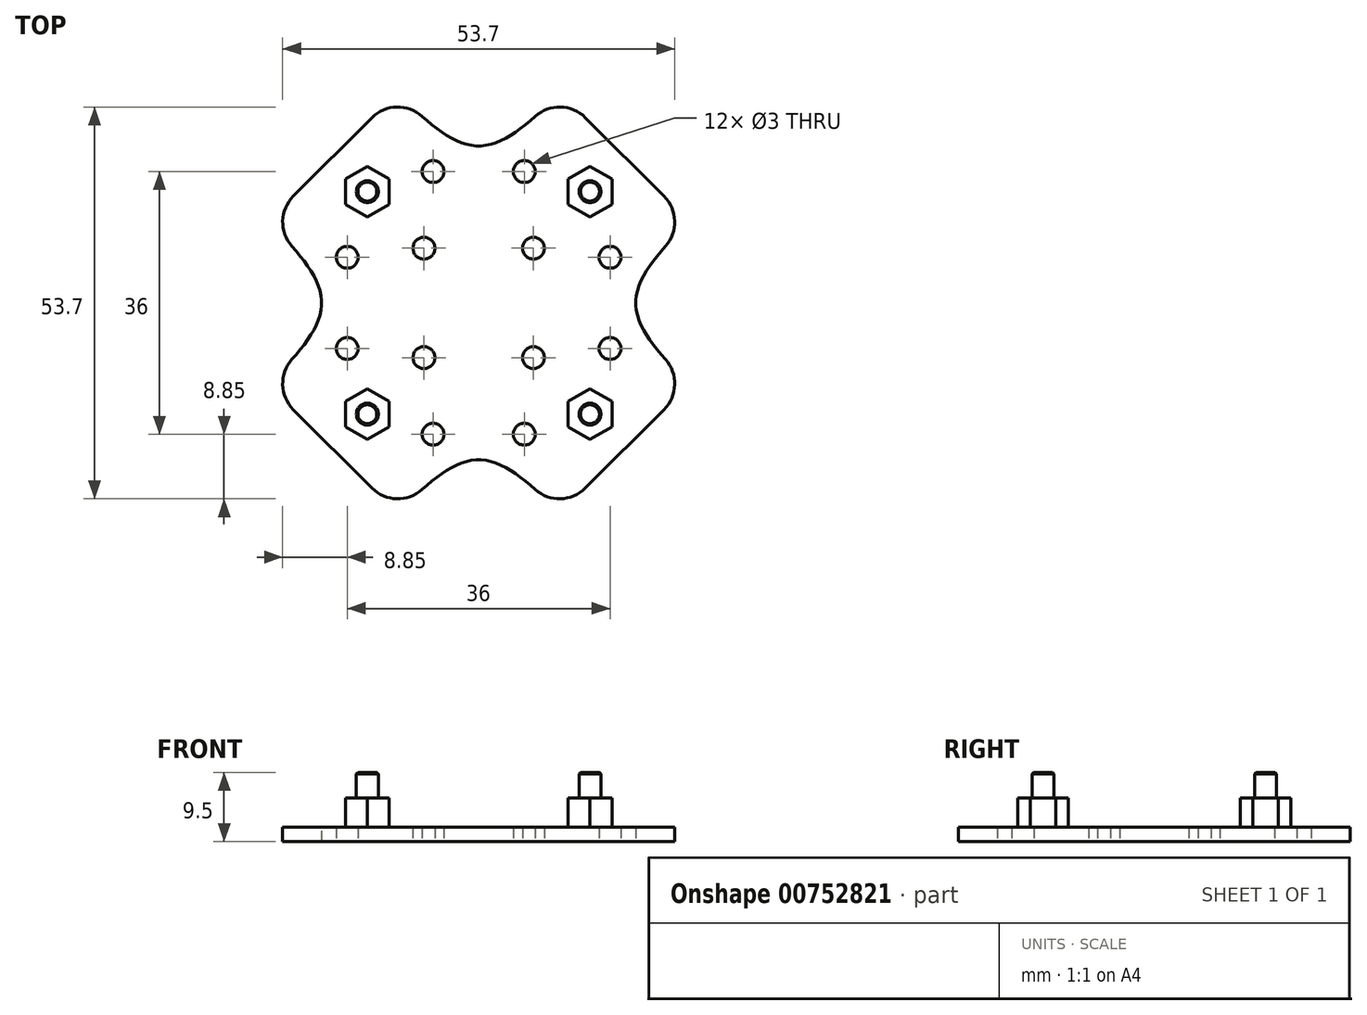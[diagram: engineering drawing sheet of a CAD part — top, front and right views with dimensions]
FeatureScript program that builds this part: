
annotation { "Feature Type Name" : "Feature", "Feature Type Description" : "" }
export const myFeature = defineFeature(function(context is Context, id is Id, definition is map)
    precondition{}
    {
        {
            var Q0;
            Q0=qCreatedBy(makeId("Top.planeOp"),FACE);
            var sketch = newSketch(context, id + "F0", { "sketchPlane" : qUnion([Q0])});
            skLineSegment(sketch, "E0.bottom", {"start": v(18, 18) * mm, "end": v(-18, 18) * mm, "construction": true});
            skLineSegment(sketch, "E0.top", {"start": v(18, -18) * mm, "end": v(-18, -18) * mm, "construction": true});
            skLineSegment(sketch, "E0.left", {"start": v(18, 18) * mm, "end": v(18, -18) * mm, "construction": true});
            skLineSegment(sketch, "E0.right", {"start": v(-18, 18) * mm, "end": v(-18, -18) * mm, "construction": true});
            skPoint(sketch, "E0.middle", {"position": v(0, 0) * mm});
            skLineSegment(sketch, "E1.bottom", {"start": v(15.25, 15.25) * mm, "end": v(-15.25, 15.25) * mm, "construction": true});
            skLineSegment(sketch, "E1.top", {"start": v(15.25, -15.25) * mm, "end": v(-15.25, -15.25) * mm, "construction": true});
            skLineSegment(sketch, "E1.left", {"start": v(15.25, 15.25) * mm, "end": v(15.25, -15.25) * mm, "construction": true});
            skLineSegment(sketch, "E1.right", {"start": v(-15.25, 15.25) * mm, "end": v(-15.25, -15.25) * mm, "construction": true});
            skCircle(sketch, "E2", {"center": v(-15.25, 15.25) * mm, "radius": 1.5 * mm});
            skCircle(sketch, "E3", {"center": v(15.25, 15.25) * mm, "radius": 1.5 * mm});
            skCircle(sketch, "E4", {"center": v(15.25, -15.25) * mm, "radius": 1.5 * mm});
            skCircle(sketch, "E5", {"center": v(-15.25, -15.25) * mm, "radius": 1.5 * mm});
            skLineSegment(sketch, "E6", {"start": v(0, 0) * mm, "end": v(-67.18, 67.18) * mm, "construction": true});
            skLineSegment(sketch, "E7", {"start": v(0, 0) * mm, "end": v(67.18, 67.18) * mm, "construction": true});
            skLineSegment(sketch, "E8", {"start": v(0, 0) * mm, "end": v(-67.18, -67.18) * mm, "construction": true});
            skLineSegment(sketch, "E9", {"start": v(0, 0) * mm, "end": v(67.18, -67.18) * mm, "construction": true});
            skCircle(sketch, "E10", {"center": v(-67.18, 67.18) * mm, "radius": 5 * mm});
            skCircle(sketch, "E11", {"center": v(-75.18, 67.18) * mm, "radius": 1.65 * mm});
            skCircle(sketch, "E12", {"center": v(-67.18, 76.68) * mm, "radius": 1.65 * mm});
            skCircle(sketch, "E13", {"center": v(-59.18, 67.18) * mm, "radius": 1.65 * mm});
            skCircle(sketch, "E14", {"center": v(-67.18, 57.68) * mm, "radius": 1.65 * mm});
            skCircle(sketch, "E15", {"center": v(67.18, 67.18) * mm, "radius": 5 * mm});
            skCircle(sketch, "E16", {"center": v(59.18, 67.18) * mm, "radius": 1.65 * mm});
            skCircle(sketch, "E17", {"center": v(67.18, 76.68) * mm, "radius": 1.65 * mm});
            skCircle(sketch, "E18", {"center": v(75.18, 67.18) * mm, "radius": 1.65 * mm});
            skCircle(sketch, "E19", {"center": v(67.18, 57.68) * mm, "radius": 1.65 * mm});
            skCircle(sketch, "E20", {"center": v(67.18, -67.18) * mm, "radius": 5 * mm});
            skCircle(sketch, "E21", {"center": v(59.18, -67.18) * mm, "radius": 1.65 * mm});
            skCircle(sketch, "E22", {"center": v(67.18, -57.68) * mm, "radius": 1.65 * mm});
            skCircle(sketch, "E23", {"center": v(75.18, -67.18) * mm, "radius": 1.65 * mm});
            skCircle(sketch, "E24", {"center": v(67.18, -76.68) * mm, "radius": 1.65 * mm});
            skCircle(sketch, "E25", {"center": v(-67.18, -67.18) * mm, "radius": 5 * mm});
            skCircle(sketch, "E26", {"center": v(-75.18, -67.18) * mm, "radius": 1.65 * mm});
            skCircle(sketch, "E27", {"center": v(-67.18, -57.68) * mm, "radius": 1.65 * mm});
            skCircle(sketch, "E28", {"center": v(-59.18, -67.18) * mm, "radius": 1.65 * mm});
            skCircle(sketch, "E29", {"center": v(-67.18, -76.68) * mm, "radius": 1.65 * mm});
            skCircle(sketch, "E30", {"center": v(-67.18, 67.18) * mm, "radius": 13.3 * mm, "construction": true});
            skCircle(sketch, "E31", {"center": v(-67.18, 67.18) * mm, "radius": 15.25 * mm});
            skCircle(sketch, "E32", {"center": v(67.18, 67.18) * mm, "radius": 13.3 * mm, "construction": true});
            skCircle(sketch, "E33", {"center": v(67.18, 67.18) * mm, "radius": 15.25 * mm});
            skCircle(sketch, "E34", {"center": v(-67.18, -67.18) * mm, "radius": 13.3 * mm, "construction": true});
            skCircle(sketch, "E35", {"center": v(-67.18, -67.18) * mm, "radius": 15.25 * mm});
            skCircle(sketch, "E36", {"center": v(67.18, -67.18) * mm, "radius": 13.3 * mm, "construction": true});
            skCircle(sketch, "E37", {"center": v(67.18, -67.18) * mm, "radius": 15.25 * mm});
            skLineSegment(sketch, "E38.bottom", {"start": v(20, 20) * mm, "end": v(-20, 20) * mm, "construction": true});
            skLineSegment(sketch, "E38.top", {"start": v(20, -20) * mm, "end": v(-20, -20) * mm, "construction": true});
            skLineSegment(sketch, "E38.left", {"start": v(20, 20) * mm, "end": v(20, -20) * mm, "construction": true});
            skLineSegment(sketch, "E38.right", {"start": v(-20, 20) * mm, "end": v(-20, -20) * mm, "construction": true});
            skLineSegment(sketch, "E39", {"start": v(-67.18, 67.18) * mm, "end": v(-77.96, 56.4) * mm, "construction": true});
            skLineSegment(sketch, "E40", {"start": v(-67.18, 67.18) * mm, "end": v(-56.4, 77.96) * mm, "construction": true});
            skPoint(sketch, "E41", {"position": v(0, 20) * mm});
            skPoint(sketch, "E42", {"position": v(-20, 0) * mm});
            skFitSpline(sketch, "E43", {"points": [v(-77.96, 56.4) * mm, v(-20, 0) * mm], "startDerivative": vector(73.8, -34.55) * mm, "endDerivative": vector(31.31, -75.4) * mm});
            skFitSpline(sketch, "E44", {"points": [v(-56.4, 77.96) * mm, v(0, 20) * mm], "startDerivative": vector(34.55, -73.8) * mm, "endDerivative": vector(75.4, -31.31) * mm});
            skLineSegment(sketch, "E45", {"start": v(67.18, 67.18) * mm, "end": v(56.4, 77.96) * mm, "construction": true});
            skLineSegment(sketch, "E46", {"start": v(67.18, 67.18) * mm, "end": v(77.96, 56.4) * mm, "construction": true});
            skFitSpline(sketch, "E47", {"points": [v(56.4, 77.96) * mm, v(0, 20) * mm], "startDerivative": vector(-34.5, -73.75) * mm, "endDerivative": vector(-75.31, -31.22) * mm});
            skFitSpline(sketch, "E48", {"points": [v(77.96, 56.4) * mm, v(20, 0) * mm], "startDerivative": vector(-73.75, -34.5) * mm, "endDerivative": vector(-31.22, -75.31) * mm});
            skCircle(sketch, "E49", {"center": v(-67.18, 67.18) * mm, "radius": 63.5 * mm, "construction": true});
            skCircle(sketch, "E50", {"center": v(67.18, 67.18) * mm, "radius": 63.5 * mm, "construction": true});
            skCircle(sketch, "E51", {"center": v(-67.18, -67.18) * mm, "radius": 63.5 * mm, "construction": true});
            skCircle(sketch, "E52", {"center": v(67.18, -67.18) * mm, "radius": 63.5 * mm, "construction": true});
            skLineSegment(sketch, "E53", {"start": v(67.18, -67.18) * mm, "end": v(56.4, -77.96) * mm, "construction": true});
            skLineSegment(sketch, "E54", {"start": v(67.18, -67.18) * mm, "end": v(77.96, -56.4) * mm, "construction": true});
            skLineSegment(sketch, "E55", {"start": v(-67.18, -67.18) * mm, "end": v(-77.96, -56.4) * mm, "construction": true});
            skLineSegment(sketch, "E56", {"start": v(-67.18, -67.18) * mm, "end": v(-56.4, -77.96) * mm, "construction": true});
            skFitSpline(sketch, "E57", {"points": [v(-77.96, -56.4) * mm, v(-20, 0) * mm], "startDerivative": vector(73.75, 34.5) * mm, "endDerivative": vector(31.22, 75.31) * mm});
            skFitSpline(sketch, "E58", {"points": [v(0, -20) * mm, v(-56.4, -77.96) * mm], "startDerivative": vector(-75.31, -31.22) * mm, "endDerivative": vector(-34.5, -73.75) * mm});
            skFitSpline(sketch, "E59", {"points": [v(0, -20) * mm, v(56.4, -77.96) * mm], "startDerivative": vector(75.31, -31.22) * mm, "endDerivative": vector(34.5, -73.75) * mm});
            skFitSpline(sketch, "E60", {"points": [v(20, 0) * mm, v(77.96, -56.4) * mm], "startDerivative": vector(31.22, -75.31) * mm, "endDerivative": vector(73.75, -34.5) * mm});
            skLineSegment(sketch, "E61", {"start": v(-20, 0) * mm, "end": v(20, 0) * mm});
            skLineSegment(sketch, "E62", {"start": v(0, 20) * mm, "end": v(0, -20) * mm});
            skLineSegment(sketch, "E63.bottom", {"start": v(-7.5, 7.5) * mm, "end": v(7.5, 7.5) * mm, "construction": true});
            skLineSegment(sketch, "E63.top", {"start": v(-7.5, -7.5) * mm, "end": v(7.5, -7.5) * mm, "construction": true});
            skLineSegment(sketch, "E63.left", {"start": v(-7.5, 7.5) * mm, "end": v(-7.5, -7.5) * mm, "construction": true});
            skLineSegment(sketch, "E63.right", {"start": v(7.5, 7.5) * mm, "end": v(7.5, -7.5) * mm, "construction": true});
            skCircle(sketch, "E64", {"center": v(-7.5, 7.5) * mm, "radius": 1.5 * mm});
            skCircle(sketch, "E65", {"center": v(7.5, 7.5) * mm, "radius": 1.5 * mm});
            skCircle(sketch, "E66", {"center": v(7.5, -7.5) * mm, "radius": 1.5 * mm});
            skCircle(sketch, "E67", {"center": v(-7.5, -7.5) * mm, "radius": 1.5 * mm});
            skLineSegment(sketch, "E68.bottom", {"start": v(6.25, 18) * mm, "end": v(-6.25, 18) * mm, "construction": true});
            skLineSegment(sketch, "E68.top", {"start": v(6.25, -18) * mm, "end": v(-6.25, -18) * mm, "construction": true});
            skLineSegment(sketch, "E68.left", {"start": v(6.25, 18) * mm, "end": v(6.25, -18) * mm, "construction": true});
            skLineSegment(sketch, "E68.right", {"start": v(-6.25, 18) * mm, "end": v(-6.25, -18) * mm, "construction": true});
            skCircle(sketch, "E69", {"center": v(-6.25, 18) * mm, "radius": 1.5 * mm});
            skCircle(sketch, "E70", {"center": v(6.25, 18) * mm, "radius": 1.5 * mm});
            skCircle(sketch, "E71", {"center": v(-6.25, -18) * mm, "radius": 1.5 * mm});
            skCircle(sketch, "E72", {"center": v(6.25, -18) * mm, "radius": 1.5 * mm});
            skLineSegment(sketch, "E73.bottom", {"start": v(-18, 6.25) * mm, "end": v(18, 6.25) * mm, "construction": true});
            skLineSegment(sketch, "E73.top", {"start": v(-18, -6.25) * mm, "end": v(18, -6.25) * mm, "construction": true});
            skLineSegment(sketch, "E73.left", {"start": v(-18, 6.25) * mm, "end": v(-18, -6.25) * mm, "construction": true});
            skLineSegment(sketch, "E73.right", {"start": v(18, 6.25) * mm, "end": v(18, -6.25) * mm, "construction": true});
            skCircle(sketch, "E74", {"center": v(-18, 6.25) * mm, "radius": 1.5 * mm});
            skCircle(sketch, "E75", {"center": v(-18, -6.25) * mm, "radius": 1.5 * mm});
            skCircle(sketch, "E76", {"center": v(18, 6.25) * mm, "radius": 1.5 * mm});
            skCircle(sketch, "E77", {"center": v(18, -6.25) * mm, "radius": 1.5 * mm});
            skLineSegment(sketch, "E78", {"start": v(-20, 20) * mm, "end": v(-11.16, 28.84) * mm});
            skLineSegment(sketch, "E79", {"start": v(-20, 20) * mm, "end": v(-28.84, 11.16) * mm});
            skLineSegment(sketch, "E80", {"start": v(20, 20) * mm, "end": v(11.16, 28.84) * mm});
            skLineSegment(sketch, "E81", {"start": v(20, 20) * mm, "end": v(28.84, 11.16) * mm});
            skLineSegment(sketch, "E82", {"start": v(20, -20) * mm, "end": v(28.84, -11.16) * mm});
            skLineSegment(sketch, "E83", {"start": v(20, -20) * mm, "end": v(11.16, -28.84) * mm});
            skLineSegment(sketch, "E84", {"start": v(-20, -20) * mm, "end": v(-28.84, -11.16) * mm});
            skLineSegment(sketch, "E85", {"start": v(-20, -20) * mm, "end": v(-11.16, -28.84) * mm});
            skLineSegment(sketch, "E86", {"start": v(0, -20) * mm, "end": v(0, -21.5) * mm, "construction": true});
            skLineSegment(sketch, "E87", {"start": v(-20, 0) * mm, "end": v(-21.5, 0) * mm, "construction": true});
            skLineSegment(sketch, "E88", {"start": v(0, 20) * mm, "end": v(0, 21.5) * mm, "construction": true});
            skLineSegment(sketch, "E89", {"start": v(20, 0) * mm, "end": v(21.5, 0) * mm, "construction": true});
            skFitSpline(sketch, "E90", {"points": [v(28.84, 11.16) * mm, v(21.5, 0) * mm, v(28.84, -11.16) * mm], "startDerivative": vector(-22.02, -22.32) * mm, "endDerivative": vector(22.02, -22.32) * mm});
            skFitSpline(sketch, "E91", {"points": [v(11.16, -28.84) * mm, v(0, -21.5) * mm, v(-11.16, -28.84) * mm], "startDerivative": vector(-22.32, 22.02) * mm, "endDerivative": vector(-22.32, -22.02) * mm});
            skFitSpline(sketch, "E92", {"points": [v(-28.84, -11.16) * mm, v(-21.5, 0) * mm, v(-28.84, 11.16) * mm], "startDerivative": vector(22.02, 22.32) * mm, "endDerivative": vector(-22.02, 22.32) * mm});
            skFitSpline(sketch, "E93", {"points": [v(-11.16, 28.84) * mm, v(0, 21.5) * mm, v(11.16, 28.84) * mm], "startDerivative": vector(22.32, -22.02) * mm, "endDerivative": vector(22.32, 22.02) * mm});
            skLineSegment(sketch, "E94", {"start": v(-15.25, 0) * mm, "end": v(-13.75, 0) * mm, "construction": true});
            skPoint(sketch, "E95.middle", {"position": v(-13.75, 0) * mm});
            skLineSegment(sketch, "E96", {"start": v(15.25, 0) * mm, "end": v(13.75, 0) * mm, "construction": true});
            skPoint(sketch, "E97.middle", {"position": v(13.75, 0) * mm});
            skCircle(sketch, "E98.cCircle", {"center": v(-15.25, 15.25) * mm, "radius": 3 * mm, "construction": true});
            skLineSegment(sketch, "E98.0", {"start": v(-12.25, 16.98) * mm, "end": v(-12.25, 13.52) * mm});
            skLineSegment(sketch, "E98.1", {"start": v(-12.25, 13.52) * mm, "end": v(-15.25, 11.79) * mm});
            skLineSegment(sketch, "E98.2", {"start": v(-15.25, 11.79) * mm, "end": v(-18.25, 13.52) * mm});
            skLineSegment(sketch, "E98.3", {"start": v(-18.25, 13.52) * mm, "end": v(-18.25, 16.98) * mm});
            skLineSegment(sketch, "E98.4", {"start": v(-18.25, 16.98) * mm, "end": v(-15.25, 18.71) * mm});
            skLineSegment(sketch, "E98.5", {"start": v(-15.25, 18.71) * mm, "end": v(-12.25, 16.98) * mm});
            skPoint(sketch, "E98.0.midPoint", {"position": v(-12.25, 15.25) * mm});
            skCircle(sketch, "E99.cCircle", {"center": v(15.25, 15.25) * mm, "radius": 3 * mm, "construction": true});
            skLineSegment(sketch, "E99.0", {"start": v(12.25, 13.52) * mm, "end": v(12.25, 16.98) * mm});
            skLineSegment(sketch, "E99.1", {"start": v(12.25, 16.98) * mm, "end": v(15.25, 18.71) * mm});
            skLineSegment(sketch, "E99.2", {"start": v(15.25, 18.71) * mm, "end": v(18.25, 16.98) * mm});
            skLineSegment(sketch, "E99.3", {"start": v(18.25, 16.98) * mm, "end": v(18.25, 13.52) * mm});
            skLineSegment(sketch, "E99.4", {"start": v(18.25, 13.52) * mm, "end": v(15.25, 11.79) * mm});
            skLineSegment(sketch, "E99.5", {"start": v(15.25, 11.79) * mm, "end": v(12.25, 13.52) * mm});
            skPoint(sketch, "E99.0.midPoint", {"position": v(12.25, 15.25) * mm});
            skCircle(sketch, "E100.cCircle", {"center": v(-15.25, -15.25) * mm, "radius": 3 * mm, "construction": true});
            skLineSegment(sketch, "E100.0", {"start": v(-12.25, -13.52) * mm, "end": v(-12.25, -16.98) * mm});
            skLineSegment(sketch, "E100.1", {"start": v(-12.25, -16.98) * mm, "end": v(-15.25, -18.71) * mm});
            skLineSegment(sketch, "E100.2", {"start": v(-15.25, -18.71) * mm, "end": v(-18.25, -16.98) * mm});
            skLineSegment(sketch, "E100.3", {"start": v(-18.25, -16.98) * mm, "end": v(-18.25, -13.52) * mm});
            skLineSegment(sketch, "E100.4", {"start": v(-18.25, -13.52) * mm, "end": v(-15.25, -11.79) * mm});
            skLineSegment(sketch, "E100.5", {"start": v(-15.25, -11.79) * mm, "end": v(-12.25, -13.52) * mm});
            skPoint(sketch, "E100.0.midPoint", {"position": v(-12.25, -15.25) * mm});
            skPoint(sketch, "E101.0.midPoint", {"position": v(12.25, -15.25) * mm});
            skCircle(sketch, "E102.cCircle", {"center": v(15.25, -15.25) * mm, "radius": 3 * mm, "construction": true});
            skLineSegment(sketch, "E102.0", {"start": v(12.25, -16.98) * mm, "end": v(12.25, -13.52) * mm});
            skLineSegment(sketch, "E102.1", {"start": v(12.25, -13.52) * mm, "end": v(15.25, -11.79) * mm});
            skLineSegment(sketch, "E102.2", {"start": v(15.25, -11.79) * mm, "end": v(18.25, -13.52) * mm});
            skLineSegment(sketch, "E102.3", {"start": v(18.25, -13.52) * mm, "end": v(18.25, -16.98) * mm});
            skLineSegment(sketch, "E102.4", {"start": v(18.25, -16.98) * mm, "end": v(15.25, -18.71) * mm});
            skLineSegment(sketch, "E102.5", {"start": v(15.25, -18.71) * mm, "end": v(12.25, -16.98) * mm});
            skSolve(sketch);
        }
        {
            var Q0;
            Q0=makeQuery(id+"F0.imprint","IMPRINT",FACE,{"disambiguationData":[TD([[makeQuery(id+"F0.imprint","IMPRINT",EDGE,{"derivedFrom":sQuery(id+"F0.wireOp",EDGE,"E64")}),-1.0]])]});
            var Q1;
            Q1=makeQuery(id+"F0.imprint","IMPRINT",FACE,{"disambiguationData":[TD([[makeQuery(id+"F0.imprint","IMPRINT",EDGE,{"derivedFrom":sQuery(id+"F0.wireOp",EDGE,"E67")}),-1.0]])]});
            var Q2;
            {var subQ0=sQuery(id+"F0.wireOp",EDGE,"E93");Q2=makeQuery(id+"F0.imprint","IMPRINT",FACE,{"disambiguationData":[TD([[makeQuery(id+"F0.imprint","IMPRINT",EDGE,{"derivedFrom":subQ0}),-1.0]])]});}
            var Q3;
            {var subQ0=sQuery(id+"F0.wireOp",EDGE,"E92");Q3=makeQuery(id+"F0.imprint","IMPRINT",FACE,{"disambiguationData":[TD([[makeQuery(id+"F0.imprint","IMPRINT",EDGE,{"derivedFrom":subQ0}),-1.0]])]});}
            var Q4;
            {var subQ0=sQuery(id+"F0.wireOp",EDGE,"E90");Q4=makeQuery(id+"F0.imprint","IMPRINT",FACE,{"disambiguationData":[TD([[makeQuery(id+"F0.imprint","IMPRINT",EDGE,{"derivedFrom":subQ0}),-1.0]])]});}
            var Q5;
            Q5=makeQuery(id+"F0.imprint","IMPRINT",FACE,{"disambiguationData":[TD([[makeQuery(id+"F0.imprint","IMPRINT",EDGE,{"derivedFrom":sQuery(id+"F0.wireOp",EDGE,"E66")}),-1.0]])]});
            var Q6;
            {var subQ0=sQuery(id+"F0.wireOp",EDGE,"E91");Q6=makeQuery(id+"F0.imprint","IMPRINT",FACE,{"disambiguationData":[TD([[makeQuery(id+"F0.imprint","IMPRINT",EDGE,{"derivedFrom":subQ0}),-1.0]])]});}
            var Q7;
            Q7=makeQuery(id+"F0.imprint","IMPRINT",FACE,{"disambiguationData":[TD([[makeQuery(id+"F0.imprint","IMPRINT",EDGE,{"derivedFrom":sQuery(id+"F0.wireOp",EDGE,"E65")}),-1.0]])]});
            var Q8;
            Q8=makeQuery(id+"F0.imprint","IMPRINT",FACE,{"disambiguationData":[TD([[makeQuery(id+"F0.imprint","IMPRINT",EDGE,{"derivedFrom":sQuery(id+"F0.wireOp",EDGE,"E2")}),-1.0]])]});
            var Q9;
            Q9=makeQuery(id+"F0.imprint","IMPRINT",FACE,{"disambiguationData":[TD([[makeQuery(id+"F0.imprint","IMPRINT",EDGE,{"derivedFrom":sQuery(id+"F0.wireOp",EDGE,"E2")}),1.0]])]});
            var Q10;
            Q10=makeQuery(id+"F0.imprint","IMPRINT",FACE,{"disambiguationData":[TD([[makeQuery(id+"F0.imprint","IMPRINT",EDGE,{"derivedFrom":sQuery(id+"F0.wireOp",EDGE,"E3")}),-1.0]])]});
            var Q11;
            Q11=makeQuery(id+"F0.imprint","IMPRINT",FACE,{"disambiguationData":[TD([[makeQuery(id+"F0.imprint","IMPRINT",EDGE,{"derivedFrom":sQuery(id+"F0.wireOp",EDGE,"E3")}),1.0]])]});
            var Q12;
            Q12=makeQuery(id+"F0.imprint","IMPRINT",FACE,{"disambiguationData":[TD([[makeQuery(id+"F0.imprint","IMPRINT",EDGE,{"derivedFrom":sQuery(id+"F0.wireOp",EDGE,"E4")}),-1.0]])]});
            var Q13;
            Q13=makeQuery(id+"F0.imprint","IMPRINT",FACE,{"disambiguationData":[TD([[makeQuery(id+"F0.imprint","IMPRINT",EDGE,{"derivedFrom":sQuery(id+"F0.wireOp",EDGE,"E4")}),1.0]])]});
            var Q14;
            Q14=makeQuery(id+"F0.imprint","IMPRINT",FACE,{"disambiguationData":[TD([[makeQuery(id+"F0.imprint","IMPRINT",EDGE,{"derivedFrom":sQuery(id+"F0.wireOp",EDGE,"E5")}),-1.0]])]});
            var Q15;
            Q15=makeQuery(id+"F0.imprint","IMPRINT",FACE,{"disambiguationData":[TD([[makeQuery(id+"F0.imprint","IMPRINT",EDGE,{"derivedFrom":sQuery(id+"F0.wireOp",EDGE,"E5")}),1.0]])]});
            extrude(context, id + "F1", {"entities" : qUnion([Q0, Q1, Q2, Q3, Q4, Q5, Q6, Q7, Q8, Q9, Q10, Q11, Q12, Q13, Q14, Q15]), "depth" : 2 * mm, "offsetDistance" : 25 * mm});
        }
        {
            var Q0;
            Q0=makeQuery(id+"F1.opExtrude","SWEPT_EDGE",EDGE,{"disambiguationData":[OSD([sQuery(id+"F0.wireOp",EDGE,"E78"),sQuery(id+"F0.wireOp",EDGE,"E93")])]});
            var Q1;
            Q1=makeQuery(id+"F1.opExtrude","SWEPT_EDGE",EDGE,{"disambiguationData":[OSD([sQuery(id+"F0.wireOp",EDGE,"E79"),sQuery(id+"F0.wireOp",EDGE,"E92")])]});
            var Q2;
            Q2=makeQuery(id+"F1.opExtrude","SWEPT_EDGE",EDGE,{"disambiguationData":[OSD([sQuery(id+"F0.wireOp",EDGE,"E80"),sQuery(id+"F0.wireOp",EDGE,"E93")])]});
            var Q3;
            Q3=makeQuery(id+"F1.opExtrude","SWEPT_EDGE",EDGE,{"disambiguationData":[OSD([sQuery(id+"F0.wireOp",EDGE,"E81"),sQuery(id+"F0.wireOp",EDGE,"E90")])]});
            var Q4;
            Q4=makeQuery(id+"F1.opExtrude","SWEPT_EDGE",EDGE,{"disambiguationData":[OSD([sQuery(id+"F0.wireOp",EDGE,"E82"),sQuery(id+"F0.wireOp",EDGE,"E90")])]});
            var Q5;
            Q5=makeQuery(id+"F1.opExtrude","SWEPT_EDGE",EDGE,{"disambiguationData":[OSD([sQuery(id+"F0.wireOp",EDGE,"E83"),sQuery(id+"F0.wireOp",EDGE,"E91")])]});
            var Q6;
            Q6=makeQuery(id+"F1.opExtrude","SWEPT_EDGE",EDGE,{"disambiguationData":[OSD([sQuery(id+"F0.wireOp",EDGE,"E85"),sQuery(id+"F0.wireOp",EDGE,"E91")])]});
            var Q7;
            Q7=makeQuery(id+"F1.opExtrude","SWEPT_EDGE",EDGE,{"disambiguationData":[OSD([sQuery(id+"F0.wireOp",EDGE,"E84"),sQuery(id+"F0.wireOp",EDGE,"E92")])]});
            fillet(context, id + "F2", {"entities" : qUnion([Q0, Q1, Q2, Q3, Q4, Q5, Q6, Q7]), "radius" : 5 * mm, "tangentPropagation" : true, "allowEdgeOverflow" : false});
        }
        {
            var Q0;
            Q0=makeQuery(id+"F0.imprint","IMPRINT",FACE,{"disambiguationData":[TD([[makeQuery(id+"F0.imprint","IMPRINT",EDGE,{"derivedFrom":sQuery(id+"F0.wireOp",EDGE,"E2")}),1.0]])]});
            var Q1;
            Q1=makeQuery(id+"F0.imprint","IMPRINT",FACE,{"disambiguationData":[TD([[makeQuery(id+"F0.imprint","IMPRINT",EDGE,{"derivedFrom":sQuery(id+"F0.wireOp",EDGE,"E2")}),-1.0]])]});
            var Q2;
            Q2=makeQuery(id+"F0.imprint","IMPRINT",FACE,{"disambiguationData":[TD([[makeQuery(id+"F0.imprint","IMPRINT",EDGE,{"derivedFrom":sQuery(id+"F0.wireOp",EDGE,"E3")}),-1.0]])]});
            var Q3;
            Q3=makeQuery(id+"F0.imprint","IMPRINT",FACE,{"disambiguationData":[TD([[makeQuery(id+"F0.imprint","IMPRINT",EDGE,{"derivedFrom":sQuery(id+"F0.wireOp",EDGE,"E3")}),1.0]])]});
            var Q4;
            Q4=makeQuery(id+"F0.imprint","IMPRINT",FACE,{"disambiguationData":[TD([[makeQuery(id+"F0.imprint","IMPRINT",EDGE,{"derivedFrom":sQuery(id+"F0.wireOp",EDGE,"E4")}),1.0]])]});
            var Q5;
            Q5=makeQuery(id+"F0.imprint","IMPRINT",FACE,{"disambiguationData":[TD([[makeQuery(id+"F0.imprint","IMPRINT",EDGE,{"derivedFrom":sQuery(id+"F0.wireOp",EDGE,"E4")}),-1.0]])]});
            var Q6;
            Q6=makeQuery(id+"F0.imprint","IMPRINT",FACE,{"disambiguationData":[TD([[makeQuery(id+"F0.imprint","IMPRINT",EDGE,{"derivedFrom":sQuery(id+"F0.wireOp",EDGE,"E5")}),-1.0]])]});
            var Q7;
            Q7=makeQuery(id+"F0.imprint","IMPRINT",FACE,{"disambiguationData":[TD([[makeQuery(id+"F0.imprint","IMPRINT",EDGE,{"derivedFrom":sQuery(id+"F0.wireOp",EDGE,"E5")}),1.0]])]});
            extrude(context, id + "F3", {"entities" : qUnion([Q0, Q1, Q2, Q3, Q4, Q5, Q6, Q7]), "operationType" : NewBodyOperationType.ADD, "depth" : 6 * mm, "offsetDistance" : 25 * mm});
        }
        {
            var Q0;
            Q0=makeQuery(id+"F0.imprint","IMPRINT",FACE,{"disambiguationData":[TD([[makeQuery(id+"F0.imprint","IMPRINT",EDGE,{"derivedFrom":sQuery(id+"F0.wireOp",EDGE,"E2")}),1.0]])]});
            var Q1;
            Q1=makeQuery(id+"F0.imprint","IMPRINT",FACE,{"disambiguationData":[TD([[makeQuery(id+"F0.imprint","IMPRINT",EDGE,{"derivedFrom":sQuery(id+"F0.wireOp",EDGE,"E5")}),1.0]])]});
            var Q2;
            Q2=makeQuery(id+"F0.imprint","IMPRINT",FACE,{"disambiguationData":[TD([[makeQuery(id+"F0.imprint","IMPRINT",EDGE,{"derivedFrom":sQuery(id+"F0.wireOp",EDGE,"E3")}),1.0]])]});
            var Q3;
            Q3=makeQuery(id+"F0.imprint","IMPRINT",FACE,{"disambiguationData":[TD([[makeQuery(id+"F0.imprint","IMPRINT",EDGE,{"derivedFrom":sQuery(id+"F0.wireOp",EDGE,"E4")}),1.0]])]});
            extrude(context, id + "F4", {"entities" : qUnion([Q0, Q1, Q2, Q3]), "operationType" : NewBodyOperationType.ADD, "depth" : 9.5 * mm, "offsetDistance" : 25 * mm});
        }
        {
            var Q0;
            Q0=makeQuery(id+"F4.opExtrude","CAP_EDGE",EDGE,{"disambiguationData":[OSD([sQuery(id+"F0.wireOp",EDGE,"E5")])],"isStart":false});
            var Q1;
            Q1=makeQuery(id+"F4.opExtrude","CAP_EDGE",EDGE,{"disambiguationData":[OSD([sQuery(id+"F0.wireOp",EDGE,"E2")])],"isStart":false});
            var Q2;
            Q2=makeQuery(id+"F4.opExtrude","CAP_EDGE",EDGE,{"disambiguationData":[OSD([sQuery(id+"F0.wireOp",EDGE,"E3")])],"isStart":false});
            var Q3;
            Q3=makeQuery(id+"F4.opExtrude","CAP_EDGE",EDGE,{"disambiguationData":[OSD([sQuery(id+"F0.wireOp",EDGE,"E4")])],"isStart":false});
            chamfer(context, id + "F5", {"entities" : qUnion([Q0, Q1, Q2, Q3]), "width" : 0.2 * mm, "tangentPropagation" : true});
        }
    });
